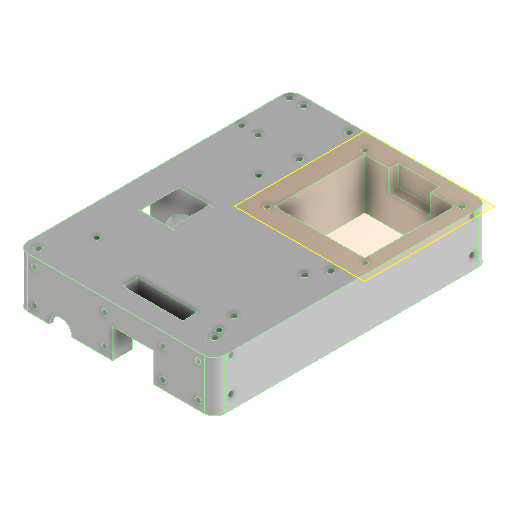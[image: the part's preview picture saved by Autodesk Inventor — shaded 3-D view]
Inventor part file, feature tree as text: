
AUTODESK INVENTOR PART (.ipt)
format: ipt  version: 2024.1 (Build 281209000, 209)  size: 492,544 bytes
history: native  units: mm
features: sketch x9, other x5, plane x2, hole x1, reference x1
ambient origin geometry x8: Origin, YZ Plane, XZ Plane, XY Plane, X Axis, Y Axis, Z Axis, Center Point
bodies: Volumenkörper1 (feature_tree)
feature tree (18):
  other  "60_Planktoscope_Base_half1.ipt"
  hole  "Bohrung1"  [1 undecoded]
  other  "Volumenkörper1::60_Planktoscope_Base_half1.ipt"
  other  "Bezeichnung1"
  sketch  "Skizze1"  dims[d0=10.0mm]
  sketch  "Skizze2"  dims[d1=2.8mm d2=6.0mm d3=4.0mm d4=2.0mm d5=90.0deg d6=12.0mm d7=20.594885mm]
  sketch  "Skizze3"
  sketch  "Skizze4"
  sketch  "Skizze5"
  sketch  "Skizze6"
  sketch  "Skizze8"
  sketch  "Skizze10"
  plane  "Arbeitsebene1"
  plane  "Arbeitsebene2"
  sketch  "Skizze12"
  reference  "Referenz5"
  other  "Assembly_Planktoscope_Uc2version_V1.iam"
  other  "00_UC2_ESP32-cnc_v3:1"
note: 1 required parameter value undecoded (feature->parameter linkage not recoverable at this tier; creation-order binding heuristic only, values carry confidence <= 0.55)
